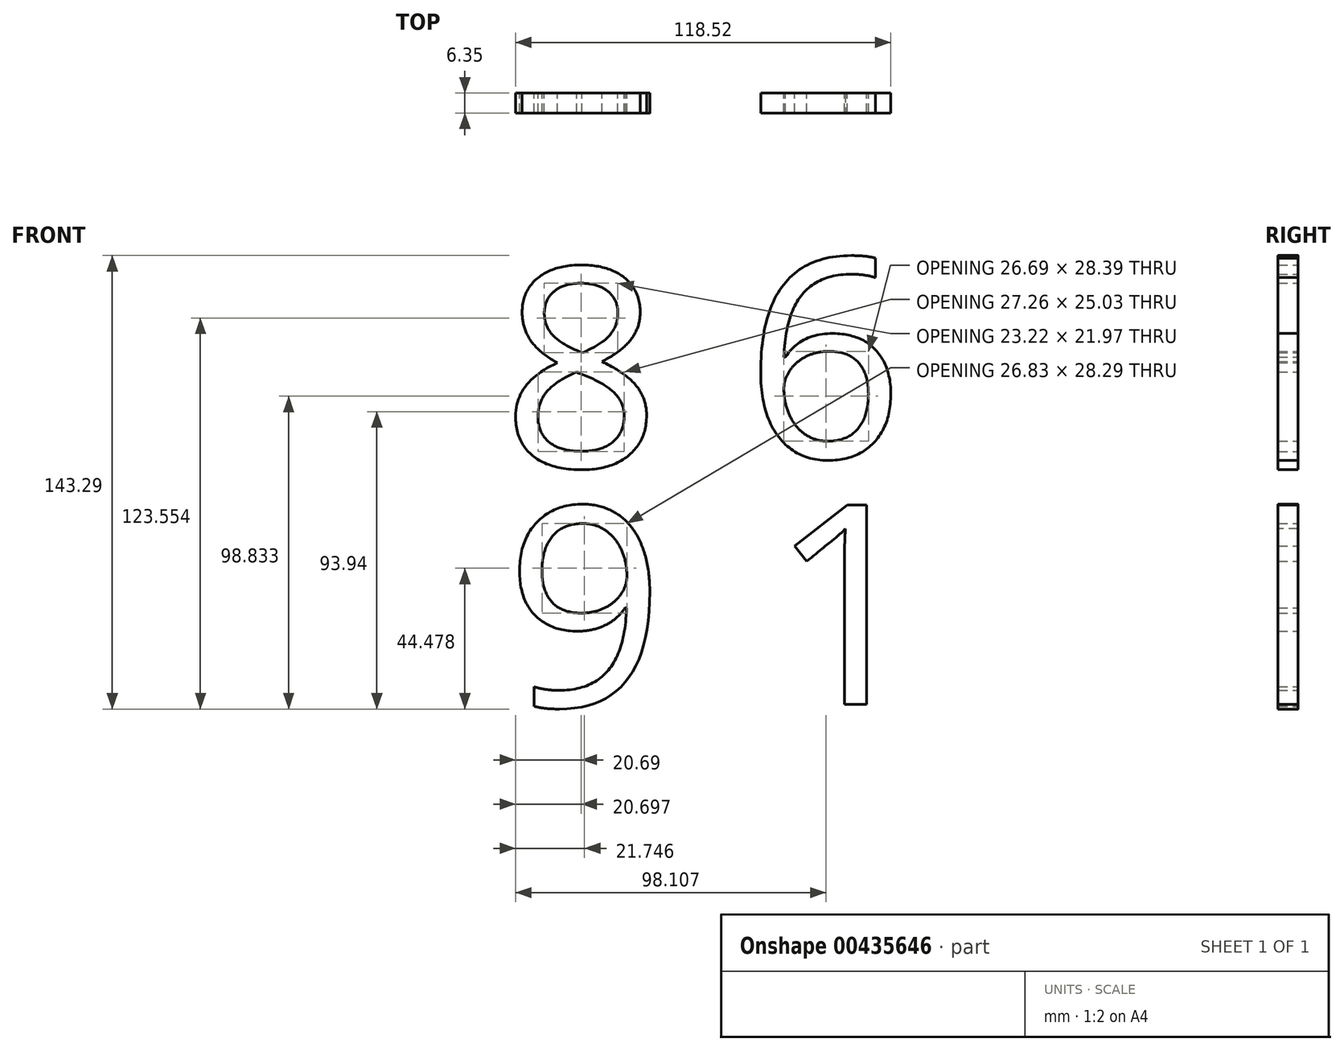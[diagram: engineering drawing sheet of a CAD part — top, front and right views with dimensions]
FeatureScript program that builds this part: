
annotation { "Feature Type Name" : "Feature", "Feature Type Description" : "" }
export const myFeature = defineFeature(function(context is Context, id is Id, definition is map)
    precondition{}
    {
        {
            var Q0;
            Q0=qCreatedBy(makeId("Front.planeOp"),FACE);
            var sketch = newSketch(context, id + "F0", { "sketchPlane" : qUnion([Q0])});
            skText(sketch, "E0", { "text": "8", "fontName": "OpenSans-Regular.ttf"});
            skText(sketch, "E1", { "text": "6\n", "fontName": "OpenSans-Regular.ttf"});
            skText(sketch, "E2", { "text": "9", "fontName": "OpenSans-Regular.ttf"});
            skText(sketch, "E3", { "text": "1", "fontName": "OpenSans-Regular.ttf"});
            const initialGuessF0  = {"E0": [-0.06448, 0.00445, 1, 0, 0.0635], "E1": [0.0124, 0.0074, 1, 0, 0.0635], "E2": [-0.0633, -0.07116, 1, 0, 0.0635], "E3": [0.02004, -0.07055, 1, 0, 0.0635]};
            skSetInitialGuess(sketch, initialGuessF0);
            skSolve(sketch);
        }
        {
            var Q0;
            Q0 = qSketchRegion(id + "F0", true);
            extrude(context, id + "F1", {"entities" : qUnion([Q0]), "depth" : 6.35 * mm});
        }
    });
